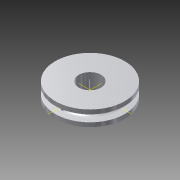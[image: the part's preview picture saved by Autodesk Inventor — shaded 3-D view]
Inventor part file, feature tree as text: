
AUTODESK INVENTOR PART (.ipt)
format: ipt  version: 2015 (Build 190159000, 159)  size: 150,528 bytes
history: native  units: mm
features: hole x2, sketch x2, revolve x1
ambient origin geometry x8: Origin, YZ Plane, XZ Plane, XY Plane, X Axis, Y Axis, Z Axis, Center Point
bodies: Solid1 (feature_tree)
feature tree (5):
  revolve  "Revolution1"  [1 undecoded]
  hole  "Hole1"  [1 undecoded]
  hole  "Hole2"  [1 undecoded]
  sketch  "Sketch1"  dims[d0=12.5mm d3=1.5mm]
  sketch  "Sketch2"  dims[d4=360.0deg d17=10.0mm d18=10.0mm d7=8.0mm d8=6.0mm d9=4.0mm d10=2.0mm d11=90.0deg d12=8.0mm d13=20.594885mm d14=5.067344mm d15=1.25mm d16=2.0mm d19=2.459mm d20=6.0mm d21=6.3mm d22=2.0mm d23=90.0deg d24=8.8mm d25=20.594885mm]
note: 3 required parameter values undecoded (feature->parameter linkage not recoverable at this tier; creation-order binding heuristic only, values carry confidence <= 0.55)